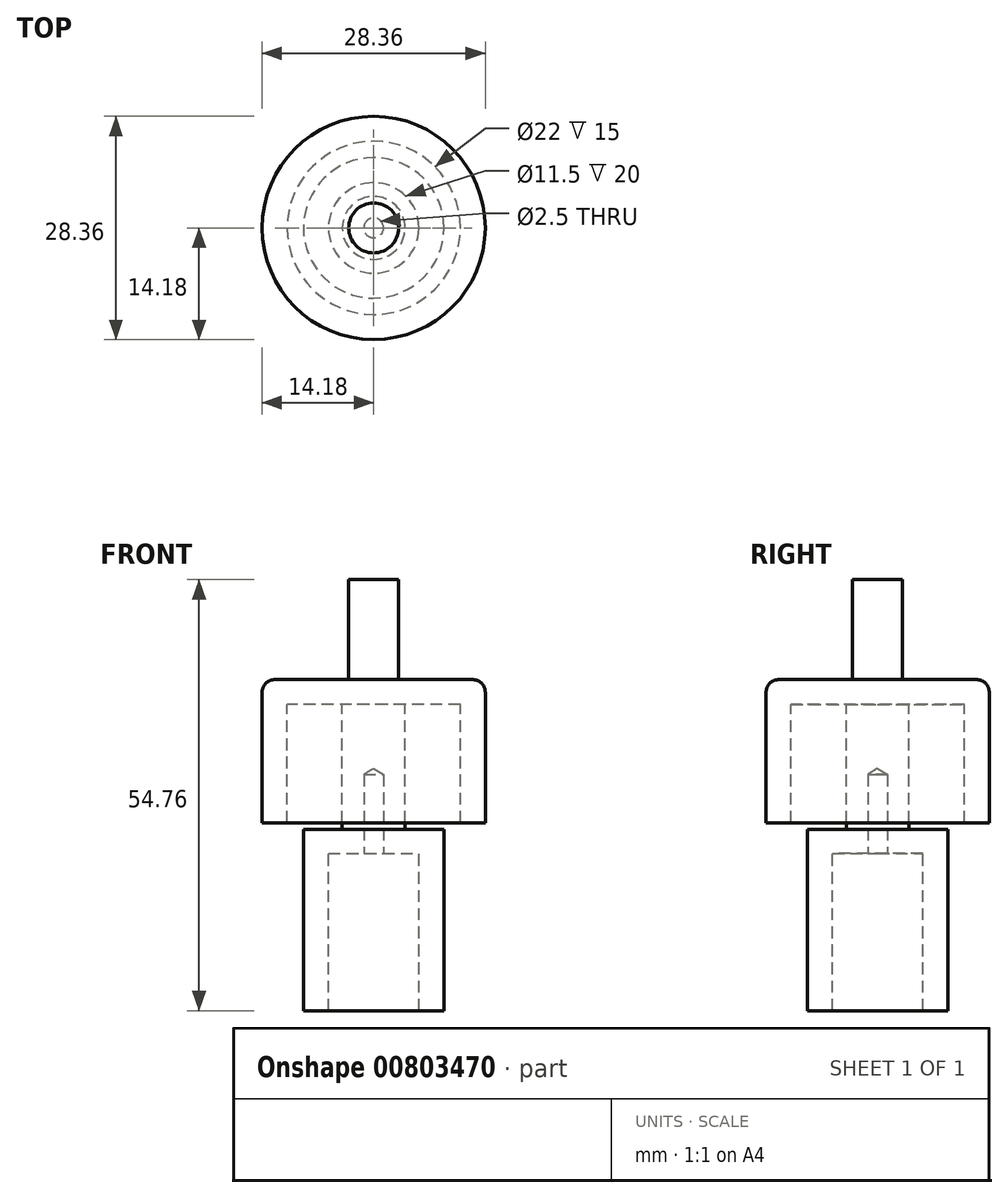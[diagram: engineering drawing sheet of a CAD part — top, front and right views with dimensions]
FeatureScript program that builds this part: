
annotation { "Feature Type Name" : "Feature", "Feature Type Description" : "" }
export const myFeature = defineFeature(function(context is Context, id is Id, definition is map)
    precondition{}
    {
        {
            var Q0;
            Q0=qCreatedBy(makeId("Top.planeOp"),FACE);
            var sketch = newSketch(context, id + "F0", { "sketchPlane" : qUnion([Q0])});
            skCircle(sketch, "E0", {"center": v(0, 0) * mm, "radius": 3.18 * mm});
            skCircle(sketch, "E1", {"center": v(0, 0) * mm, "radius": 11 * mm});
            skCircle(sketch, "E2", {"center": v(0, 0) * mm, "radius": 14.18 * mm});
            skCircle(sketch, "E3", {"center": v(0, 0) * mm, "radius": 4 * mm});
            skSolve(sketch);
        }
        {
            var Q0;
            Q0=makeQuery(id+"F0.imprint","IMPRINT",FACE,{"disambiguationData":[TD([[makeQuery(id+"F0.imprint","IMPRINT",EDGE,{"derivedFrom":sQuery(id+"F0.wireOp",EDGE,"E0")}),1.0]])]});
            extrude(context, id + "F1", {"entities" : qUnion([Q0]), "depth" : 15.88 * mm, "offsetDistance" : 25.4 * mm});
        }
        {
            var Q0;
            Q0=makeQuery(id+"F0.imprint","IMPRINT",FACE,{"disambiguationData":[TD([[makeQuery(id+"F0.imprint","IMPRINT",EDGE,{"derivedFrom":sQuery(id+"F0.wireOp",EDGE,"E1")}),-1.0]])]});
            var Q1;
            Q1=makeQuery(id+"F0.imprint","IMPRINT",FACE,{"disambiguationData":[TD([[makeQuery(id+"F0.imprint","IMPRINT",EDGE,{"derivedFrom":sQuery(id+"F0.wireOp",EDGE,"E0")}),-1.0]])]});
            var Q2;
            Q2=makeQuery(id+"F0.imprint","IMPRINT",FACE,{"disambiguationData":[TD([[makeQuery(id+"F0.imprint","IMPRINT",EDGE,{"derivedFrom":sQuery(id+"F0.wireOp",EDGE,"E1")}),1.0]])]});
            extrude(context, id + "F2", {"entities" : qUnion([Q0, Q1, Q2]), "operationType" : NewBodyOperationType.ADD, "depth" : 3.17 * mm, "offsetDistance" : 25.4 * mm});
        }
        {
            var Q0;
            Q0=makeQuery(id+"F0.imprint","IMPRINT",FACE,{"disambiguationData":[TD([[makeQuery(id+"F0.imprint","IMPRINT",EDGE,{"derivedFrom":sQuery(id+"F0.wireOp",EDGE,"E1")}),-1.0]])]});
            extrude(context, id + "F3", {"entities" : qUnion([Q0]), "operationType" : NewBodyOperationType.ADD, "oppositeDirection" : true, "depth" : 15 * mm, "offsetDistance" : 25.4 * mm});
        }
        {
            var Q0;
            Q0=makeQuery(id+"F2.opExtrude","CAP_EDGE",EDGE,{"disambiguationData":[OSD([sQuery(id+"F0.wireOp",EDGE,"E2")])],"isStart":false});
            fillet(context, id + "F4", {"entities" : qUnion([Q0]), "radius" : 1.59 * mm, "tangentPropagation" : true, "allowEdgeOverflow" : false});
        }
        {
            var Q0;
            Q0=makeQuery(id+"F0.imprint","IMPRINT",FACE,{"disambiguationData":[TD([[makeQuery(id+"F0.imprint","IMPRINT",EDGE,{"derivedFrom":sQuery(id+"F0.wireOp",EDGE,"E1")}),1.0]])]});
            var sketch = newSketch(context, id + "F5", { "sketchPlane" : qUnion([Q0])});
            skCircle(sketch, "E4.0", {"center": v(0, 0) * mm, "radius": 4 * mm});
            skSolve(sketch);
        }
        {
            var Q0;
            Q0=makeQuery(id+"F5.imprint","IMPRINT",FACE,{"disambiguationData":[TD([[makeQuery(id+"F5.imprint","IMPRINT",EDGE,{"derivedFrom":sQuery(id+"F5.wireOp",EDGE,"E4.0")}),1.0]])]});
            extrude(context, id + "F6", {"entities" : qUnion([Q0]), "oppositeDirection" : true, "depth" : 15.88 * mm, "offsetDistance" : 25.4 * mm});
        }
        {
            var Q0;
            Q0=makeQuery(id+"F6.opExtrude","CAP_FACE",FACE,{"disambiguationData":[OSD([sQuery(id+"F5.wireOp",EDGE,"E4.0")])],"isStart":false});
            var sketch = newSketch(context, id + "F7", { "sketchPlane" : qUnion([Q0])});
            skCircle(sketch, "E5", {"center": v(0, 0) * mm, "radius": 5.75 * mm});
            skCircle(sketch, "E6", {"center": v(0, 0) * mm, "radius": 8.93 * mm});
            skSolve(sketch);
        }
        {
            var Q0;
            Q0=makeQuery(id+"F7.imprint","IMPRINT",FACE,{"disambiguationData":[TD([[makeQuery(id+"F7.imprint","IMPRINT",EDGE,{"derivedFrom":sQuery(id+"F7.wireOp",EDGE,"E5")}),-1.0]])]});
            extrude(context, id + "F8", {"entities" : qUnion([Q0]), "depth" : 23 * mm, "offsetDistance" : 25.4 * mm});
        }
        {
            var Q0;
            Q0=makeQuery(id+"F7.imprint","IMPRINT",FACE,{"disambiguationData":[TD([[makeQuery(id+"F7.imprint","IMPRINT",EDGE,{"derivedFrom":makeQuery(id+"F6.opExtrude","CAP_EDGE",EDGE,{"disambiguationData":[OSD([sQuery(id+"F5.wireOp",EDGE,"E4.0")])],"isStart":false})}),-1.0]])]});
            var Q1;
            Q1=makeQuery(id+"F7.imprint","IMPRINT",FACE,{"disambiguationData":[TD([[makeQuery(id+"F7.imprint","IMPRINT",EDGE,{"derivedFrom":sQuery(id+"F7.wireOp",EDGE,"E5")}),1.0]])]});
            extrude(context, id + "F9", {"entities" : qUnion([Q0, Q1]), "operationType" : NewBodyOperationType.ADD, "depth" : 3 * mm, "offsetDistance" : 25.4 * mm});
        }
        {
            var Q0;
            Q0=makeQuery(id+"F9.opExtrude","CAP_FACE",FACE,{"disambiguationData":[OSD([sQuery(id+"F7.wireOp",EDGE,"E5")])],"isStart":false});
            var sketch = newSketch(context, id + "F10", { "sketchPlane" : qUnion([Q0])});
            skPoint(sketch, "E7", {"position": v(0, 0) * mm});
            skSolve(sketch);
        }
        {
            var Q0;
            Q0=sQuery(id+"F10.wireOp",VERTEX,"E7");
            var Q1;
            Q1=makeQuery(id+"F6.opExtrude","SWEPT_BODY",BODY,{"disambiguationData":[OSD([sQuery(id+"F5.wireOp",EDGE,"E4.0")])]});
            hole(context, id + "F11", {"style" : HoleStyle.SIMPLE, "endStyle" : HoleEndStyle.BLIND, "holeDiameter" : 2.5 * mm, "majorDiameter" : 5 * mm, "holeDepth" : 10 * mm, "isTappedThrough" : true, "tappedDepth" : 6.36 * mm, "tapClearance" : 3, "locations" : qUnion([Q0]), "scope" : qUnion([Q1])});
        }
    });
